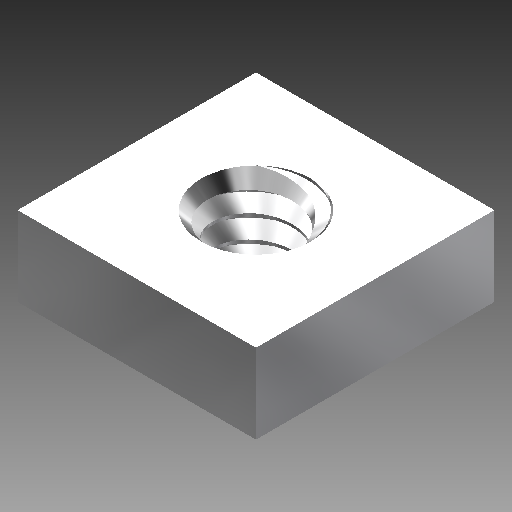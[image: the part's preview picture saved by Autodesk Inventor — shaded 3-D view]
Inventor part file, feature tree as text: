
AUTODESK INVENTOR PART (.ipt)
format: ipt  version: 2020.3 (Build 243373000, 373)  size: 229,376 bytes
history: native  units: in
note: dims shown in document units (in); Inventor stores cm internally (conversion verified against a paired STEP export)
features: mirror x1
ambient origin geometry x8: Origin, YZ Plane, XZ Plane, XY Plane, X Axis, Y Axis, Z Axis, Center Point
bodies: Solid1 (feature_tree)
feature tree (1):
  mirror  "Mirror1"
